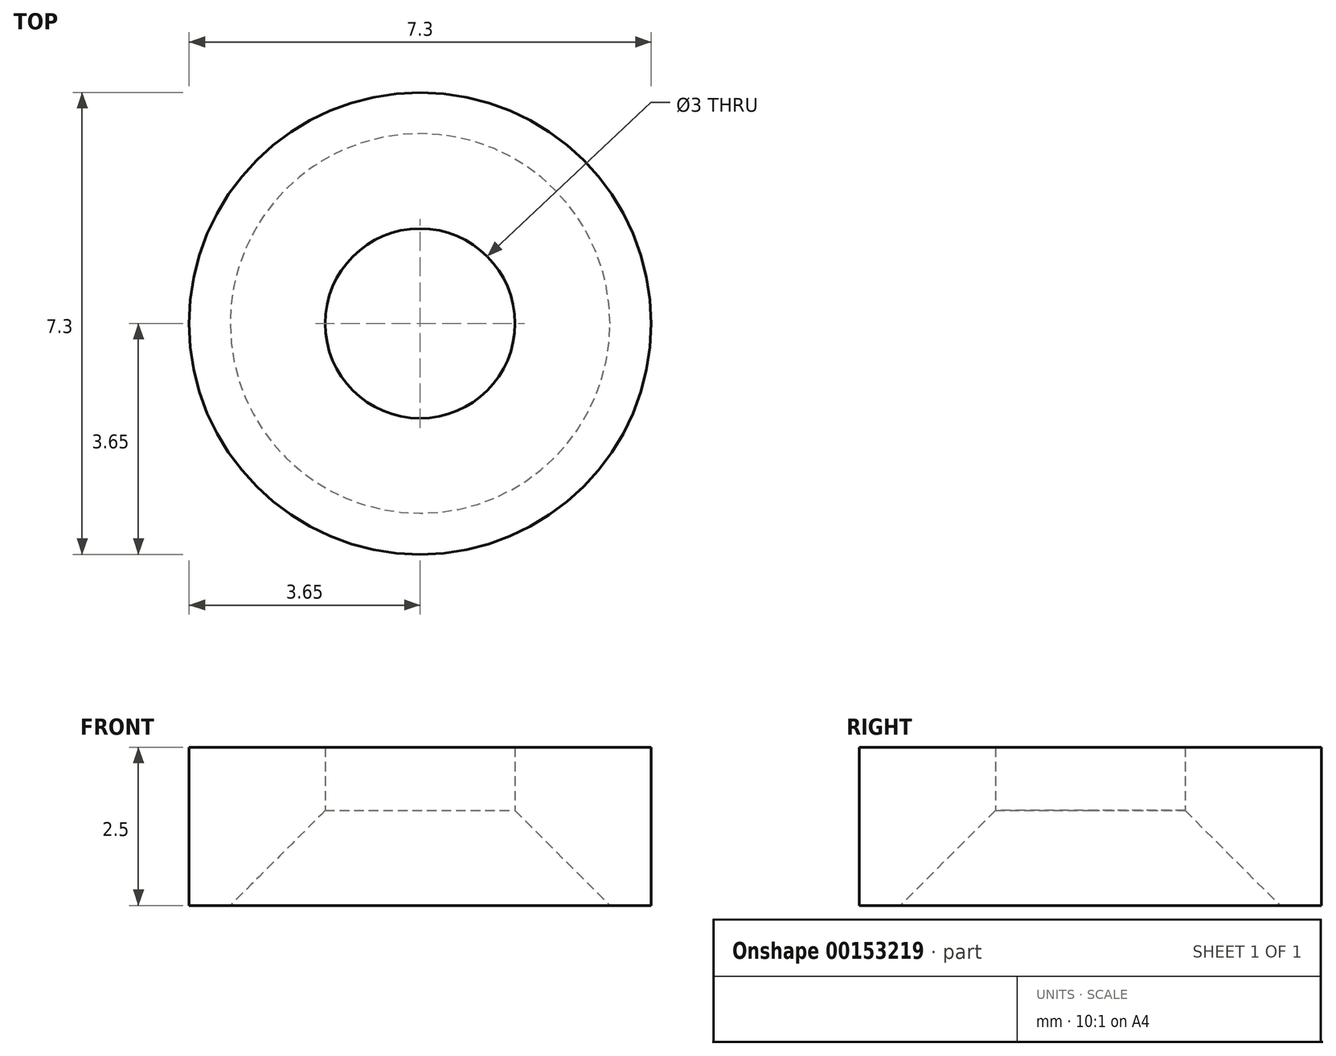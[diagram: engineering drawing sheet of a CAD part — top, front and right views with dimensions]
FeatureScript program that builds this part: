
annotation { "Feature Type Name" : "Feature", "Feature Type Description" : "" }
export const myFeature = defineFeature(function(context is Context, id is Id, definition is map)
    precondition{}
    {
        {
            var Q0;
            Q0=qCreatedBy(makeId("Top.planeOp"),FACE);
            var sketch = newSketch(context, id + "F0", { "sketchPlane" : qUnion([Q0])});
            skCircle(sketch, "E0", {"center": v(0, 0) * mm, "radius": 3.65 * mm});
            skSolve(sketch);
        }
        {
            var Q0;
            Q0 = qSketchRegion(id + "F0", true);
            extrude(context, id + "F1", {"entities" : qUnion([Q0]), "depth" : 2.5 * mm});
        }
        {
            var Q0;
            Q0=sQuery(id+"F0.wireOp",VERTEX,"E0.center");
            var Q1;
            Q1=makeQuery(id+"F1.opExtrude","SWEPT_BODY",BODY,{"disambiguationData":[OSD([sQuery(id+"F0.wireOp",EDGE,"E0")])]});
            hole(context, id + "F2", {"style" : HoleStyle.C_SINK, "endStyle" : HoleEndStyle.THROUGH, "oppositeDirection" : true, "holeDiameter" : 3 * mm, "cSinkDiameter" : 6 * mm, "cSinkAngle" : 90 * degree, "locations" : qUnion([Q0]), "scope" : qUnion([Q1]), "isTappedThrough" : true});
        }
    });
